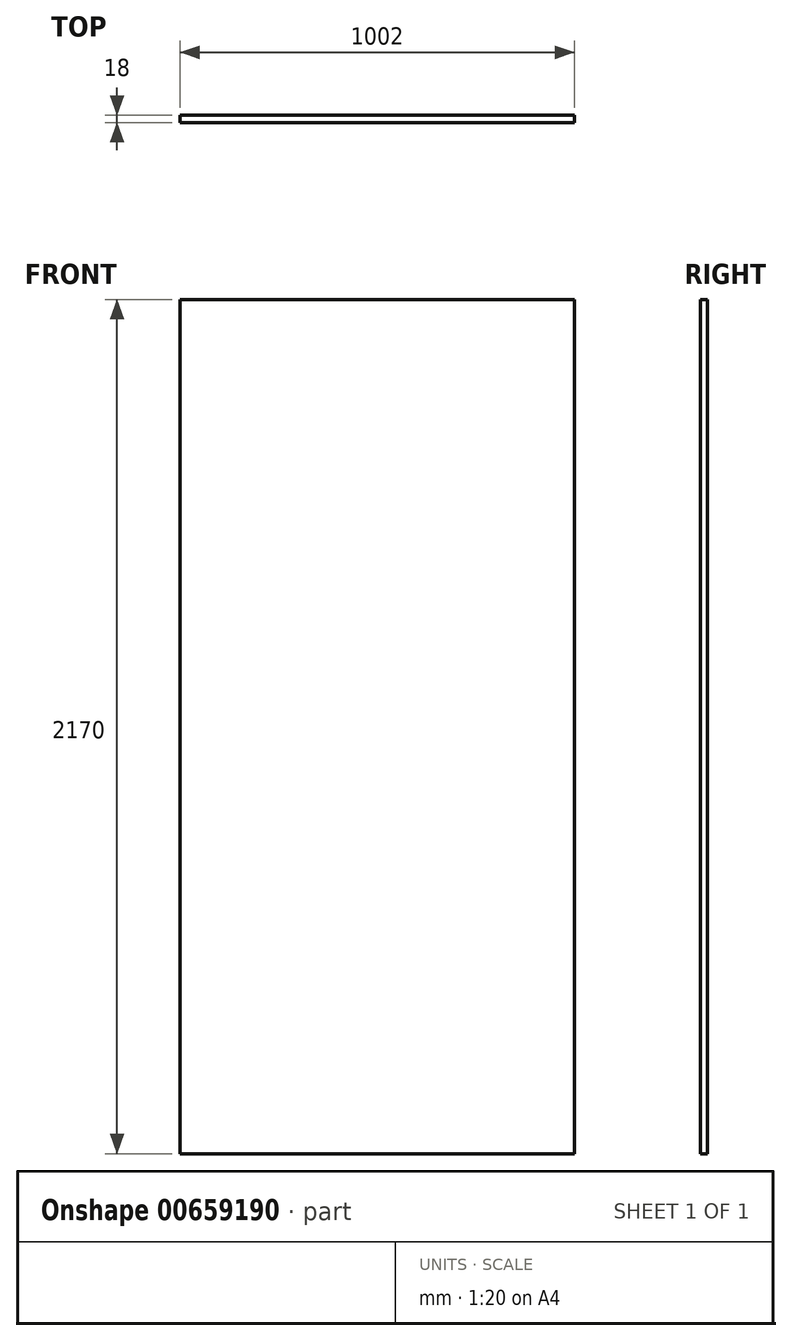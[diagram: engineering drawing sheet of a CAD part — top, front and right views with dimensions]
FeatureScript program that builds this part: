
annotation { "Feature Type Name" : "Feature", "Feature Type Description" : "" }
export const myFeature = defineFeature(function(context is Context, id is Id, definition is map)
    precondition{}
    {
        {
            var Q0;
            Q0=qCreatedBy(makeId("Front.planeOp"),FACE);
            var sketch = newSketch(context, id + "F0", { "sketchPlane" : qUnion([Q0])});
            skLineSegment(sketch, "E0.bottom", {"start": v(-501, 1085) * mm, "end": v(501, 1085) * mm});
            skLineSegment(sketch, "E0.top", {"start": v(-501, -1085) * mm, "end": v(501, -1085) * mm});
            skLineSegment(sketch, "E0.left", {"start": v(-501, 1085) * mm, "end": v(-501, -1085) * mm});
            skLineSegment(sketch, "E0.right", {"start": v(501, 1085) * mm, "end": v(501, -1085) * mm});
            skPoint(sketch, "E0.middle", {"position": v(0, 0) * mm});
            skSolve(sketch);
        }
        {
            var Q0;
            Q0=makeQuery(id+"F0.imprint","IMPRINT",FACE,{"disambiguationData":[TD([[makeQuery(id+"F0.imprint","IMPRINT",EDGE,{"derivedFrom":sQuery(id+"F0.wireOp",EDGE,"E0.bottom")}),-1.0]])]});
            extrude(context, id + "F1", {"entities" : qUnion([Q0]), "endBound" : BoundingType.SYMMETRIC, "depth" : 18 * mm, "offsetDistance" : 25 * mm});
        }
    });
